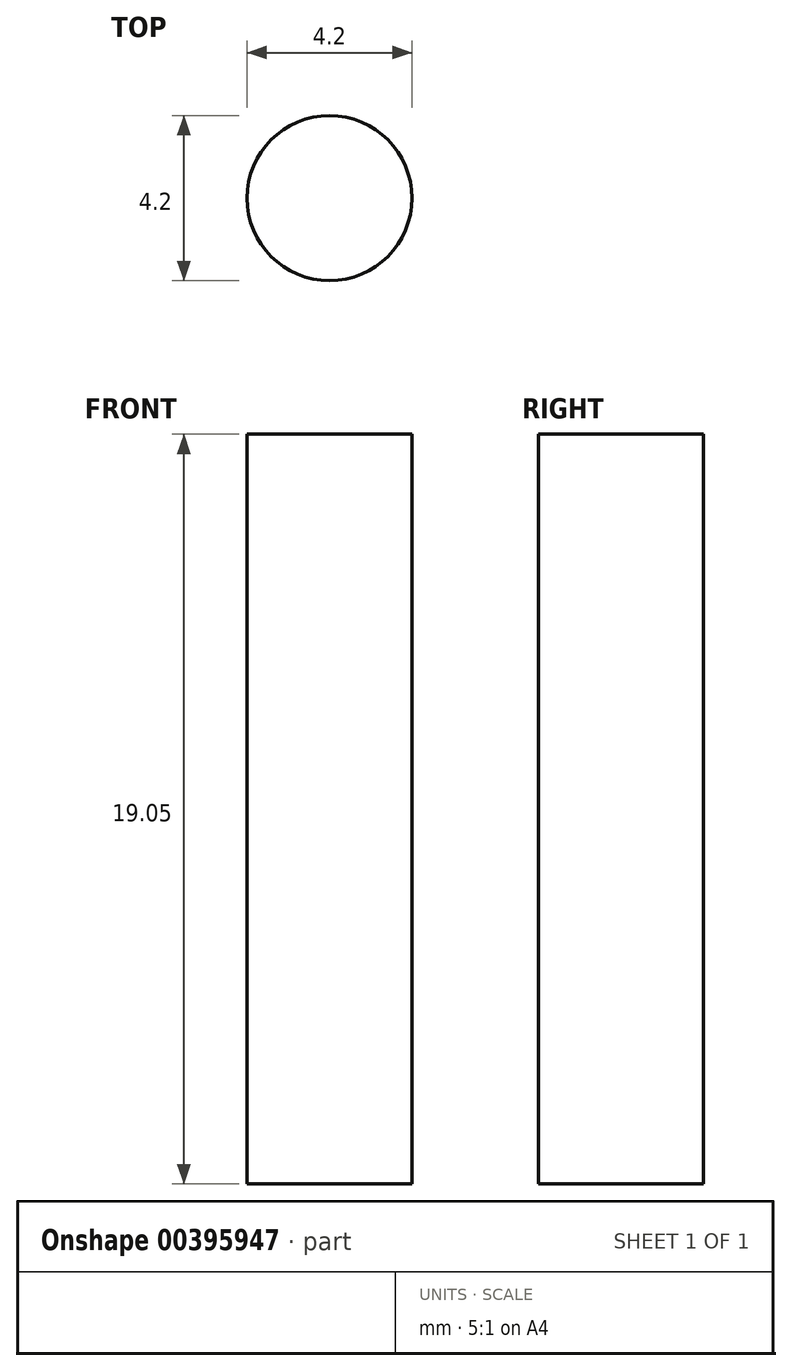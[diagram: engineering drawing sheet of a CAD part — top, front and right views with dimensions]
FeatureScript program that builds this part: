
annotation { "Feature Type Name" : "Feature", "Feature Type Description" : "" }
export const myFeature = defineFeature(function(context is Context, id is Id, definition is map)
    precondition{}
    {
        {
            var Q0;
            Q0=qCreatedBy(makeId("Top.planeOp"),FACE);
            var sketch = newSketch(context, id + "F0", { "sketchPlane" : qUnion([Q0])});
            skCircle(sketch, "E0", {"center": v(0, 0) * mm, "radius": 2.1 * mm});
            skSolve(sketch);
        }
        {
            var Q0;
            Q0=makeQuery(id+"F0.imprint","IMPRINT",FACE,{"disambiguationData":[TD([[makeQuery(id+"F0.imprint","IMPRINT",EDGE,{"derivedFrom":sQuery(id+"F0.wireOp",EDGE,"E0")}),1.0]])]});
            var Q1;
            Q1=sQuery(id+"F0.wireOp",EDGE,"E0");
            extrude(context, id + "F1", {"entities" : qUnion([Q0]), "surfaceEntities" : qUnion([Q1]), "depth" : 19.05 * mm});
        }
    });
